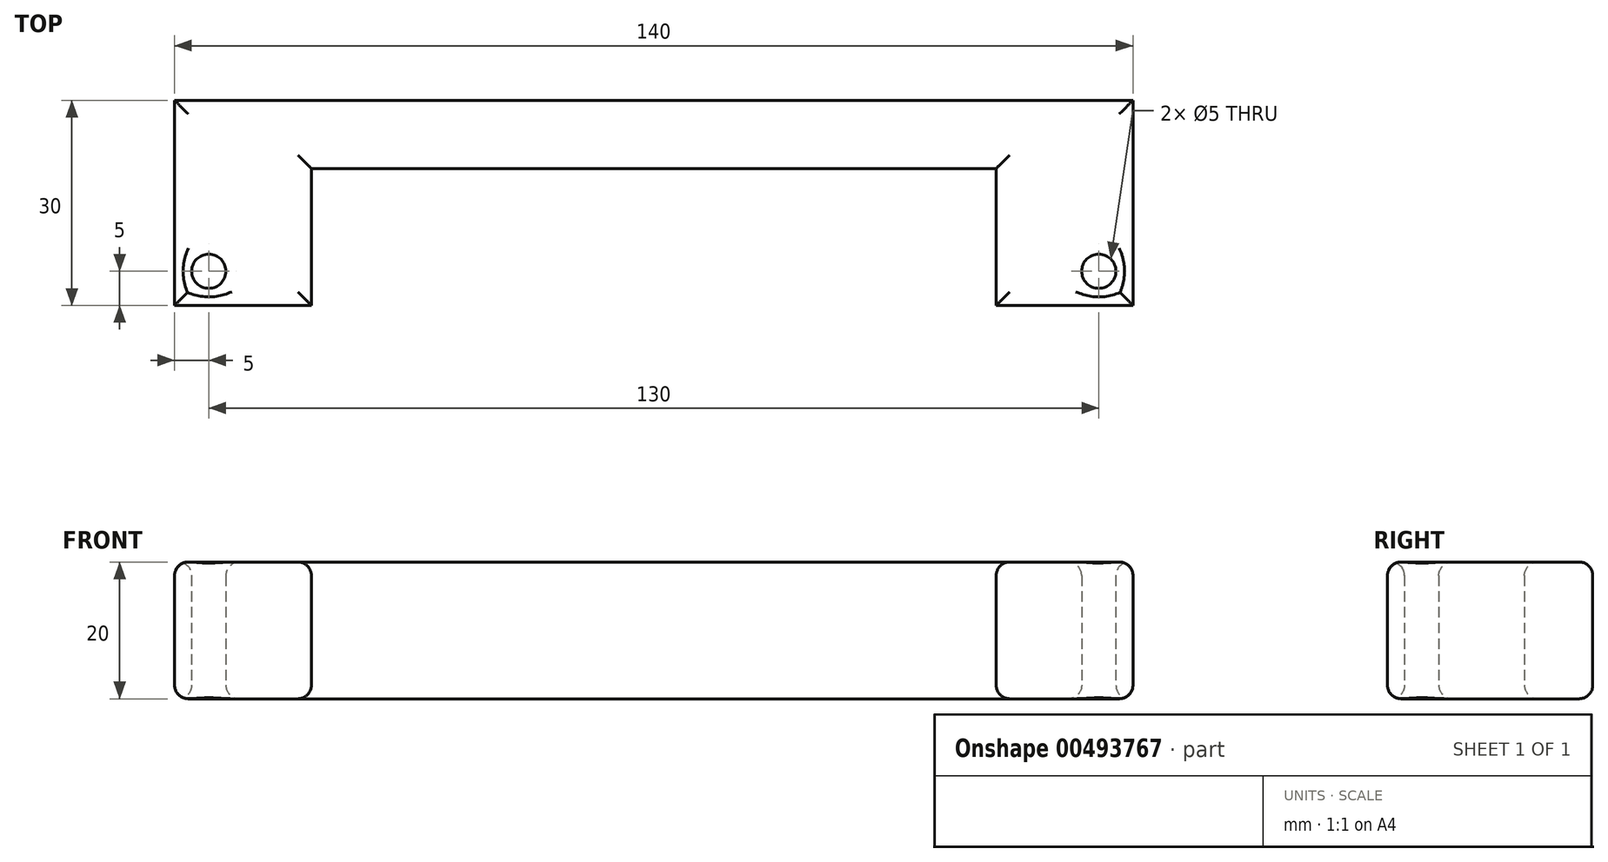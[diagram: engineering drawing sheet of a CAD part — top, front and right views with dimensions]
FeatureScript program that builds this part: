
annotation { "Feature Type Name" : "Feature", "Feature Type Description" : "" }
export const myFeature = defineFeature(function(context is Context, id is Id, definition is map)
    precondition{}
    {
        {
            var Q0;
            Q0=qCreatedBy(makeId("Top.planeOp"),FACE);
            var sketch = newSketch(context, id + "F0", { "sketchPlane" : qUnion([Q0])});
            skLineSegment(sketch, "E0", {"start": v(0, 30) * mm, "end": v(0, 20) * mm});
            skLineSegment(sketch, "E1", {"start": v(0, 20) * mm, "end": v(50, 20) * mm});
            skLineSegment(sketch, "E2", {"start": v(50, 20) * mm, "end": v(50, 0) * mm});
            skLineSegment(sketch, "E3", {"start": v(50, 0) * mm, "end": v(70, 0) * mm});
            skLineSegment(sketch, "E4", {"start": v(70, 0) * mm, "end": v(70, 30) * mm});
            skLineSegment(sketch, "E5", {"start": v(70, 30) * mm, "end": v(0, 30) * mm});
            skSolve(sketch);
        }
        {
            var Q0;
            Q0 = qSketchRegion(id + "F0", true);
            extrude(context, id + "F1", {"entities" : qUnion([Q0]), "depth" : 20 * mm});
        }
        {
            var Q0;
            Q0=qCreatedBy(makeId("Top.planeOp"),FACE);
            var sketch = newSketch(context, id + "F2", { "sketchPlane" : qUnion([Q0])});
            skPoint(sketch, "E6", {"position": v(65, 5) * mm});
            skSolve(sketch);
        }
        {
            var Q0;
            Q0=sQuery(id+"F2.wireOp",VERTEX,"E6");
            var Q1;
            Q1=makeQuery(id+"F1.opExtrude","SWEPT_BODY",BODY,{"disambiguationData":[OSD([sQuery(id+"F0.wireOp",EDGE,"E0"),sQuery(id+"F0.wireOp",EDGE,"E1"),sQuery(id+"F0.wireOp",EDGE,"E2"),sQuery(id+"F0.wireOp",EDGE,"E3"),sQuery(id+"F0.wireOp",EDGE,"E4"),sQuery(id+"F0.wireOp",EDGE,"E5")])]});
            hole(context, id + "F3", {"style" : HoleStyle.SIMPLE, "endStyle" : HoleEndStyle.THROUGH, "oppositeDirection" : true, "holeDiameter" : 5 * mm, "isTappedThrough" : true, "tappedDepth" : 12 * mm, "tapClearance" : 3, "locations" : qUnion([Q0]), "scope" : qUnion([Q1])});
        }
        {
            var Q0;
            Q0=makeQuery(id+"F1.opExtrude","SWEPT_BODY",BODY,{"disambiguationData":[OSD([sQuery(id+"F0.wireOp",EDGE,"E0"),sQuery(id+"F0.wireOp",EDGE,"E1"),sQuery(id+"F0.wireOp",EDGE,"E2"),sQuery(id+"F0.wireOp",EDGE,"E3"),sQuery(id+"F0.wireOp",EDGE,"E4"),sQuery(id+"F0.wireOp",EDGE,"E5")])]});
            var Q1;
            Q1=makeQuery(id+"F1.opExtrude","SWEPT_FACE",FACE,{"disambiguationData":[OSD([sQuery(id+"F0.wireOp",EDGE,"E0")])]});
            mirror(context, id + "F4", {"operationType" : NewBodyOperationType.ADD, "entities" : qUnion([Q0]), "mirrorPlane" : qUnion([Q1])});
        }
        {
            var Q0;
            {var subQ0=makeQuery(id+"F1.opExtrude","CAP_EDGE",EDGE,{"disambiguationData":[OSD([sQuery(id+"F0.wireOp",EDGE,"E5")])],"isStart":false});Q0=makeQuery(id+"F4.boolean.opBoolean","MERGE",EDGE,{"derivedFrom":[subQ0,makeQuery(id+"F4.opPattern","COPY",EDGE,{"derivedFrom":subQ0,"instanceName":"1"})]});}
            var Q1;
            Q1=makeQuery(id+"F1.opExtrude","CAP_EDGE",EDGE,{"disambiguationData":[OSD([sQuery(id+"F0.wireOp",EDGE,"E4")])],"isStart":false});
            var Q2;
            Q2=makeQuery(id+"F1.opExtrude","CAP_EDGE",EDGE,{"disambiguationData":[OSD([sQuery(id+"F0.wireOp",EDGE,"E2")])],"isStart":false});
            var Q3;
            {var subQ0=makeQuery(id+"F1.opExtrude","CAP_EDGE",EDGE,{"disambiguationData":[OSD([sQuery(id+"F0.wireOp",EDGE,"E1")])],"isStart":false});Q3=makeQuery(id+"F4.boolean.opBoolean","MERGE",EDGE,{"derivedFrom":[subQ0,makeQuery(id+"F4.opPattern","COPY",EDGE,{"derivedFrom":subQ0,"instanceName":"1"})]});}
            var Q4;
            Q4=makeQuery(id+"F4.opPattern","COPY",EDGE,{"derivedFrom":makeQuery(id+"F1.opExtrude","CAP_EDGE",EDGE,{"disambiguationData":[OSD([sQuery(id+"F0.wireOp",EDGE,"E2")])],"isStart":false}),"instanceName":"1"});
            var Q5;
            Q5=makeQuery(id+"F4.opPattern","COPY",EDGE,{"derivedFrom":makeQuery(id+"F1.opExtrude","CAP_EDGE",EDGE,{"disambiguationData":[OSD([sQuery(id+"F0.wireOp",EDGE,"E3")])],"isStart":false}),"instanceName":"1"});
            var Q6;
            Q6=makeQuery(id+"F4.opPattern","COPY",EDGE,{"derivedFrom":makeQuery(id+"F1.opExtrude","CAP_EDGE",EDGE,{"disambiguationData":[OSD([sQuery(id+"F0.wireOp",EDGE,"E4")])],"isStart":false}),"instanceName":"1"});
            var Q7;
            {var subQ0=makeQuery(id+"F1.opExtrude","CAP_FACE",FACE,{"disambiguationData":[OSD([sQuery(id+"F0.wireOp",EDGE,"E0"),sQuery(id+"F0.wireOp",EDGE,"E1"),sQuery(id+"F0.wireOp",EDGE,"E2"),sQuery(id+"F0.wireOp",EDGE,"E3"),sQuery(id+"F0.wireOp",EDGE,"E4"),sQuery(id+"F0.wireOp",EDGE,"E5")])],"isStart":true});Q7=makeQuery(id+"F4.boolean.opBoolean","MERGE",FACE,{"derivedFrom":[subQ0,makeQuery(id+"F4.opPattern","COPY",FACE,{"derivedFrom":subQ0,"instanceName":"1"})]});}
            var Q8;
            {var subQ0=makeQuery(id+"F1.opExtrude","CAP_FACE",FACE,{"disambiguationData":[OSD([sQuery(id+"F0.wireOp",EDGE,"E0"),sQuery(id+"F0.wireOp",EDGE,"E1"),sQuery(id+"F0.wireOp",EDGE,"E2"),sQuery(id+"F0.wireOp",EDGE,"E3"),sQuery(id+"F0.wireOp",EDGE,"E4"),sQuery(id+"F0.wireOp",EDGE,"E5")])],"isStart":false});Q8=makeQuery(id+"F4.boolean.opBoolean","MERGE",FACE,{"derivedFrom":[subQ0,makeQuery(id+"F4.opPattern","COPY",FACE,{"derivedFrom":subQ0,"instanceName":"1"})]});}
            fillet(context, id + "F5", {"entities" : qUnion([Q0, Q1, Q2, Q3, Q4, Q5, Q6, Q7, Q8]), "radius" : 2 * mm, "tangentPropagation" : true, "allowEdgeOverflow" : false});
        }
    });
